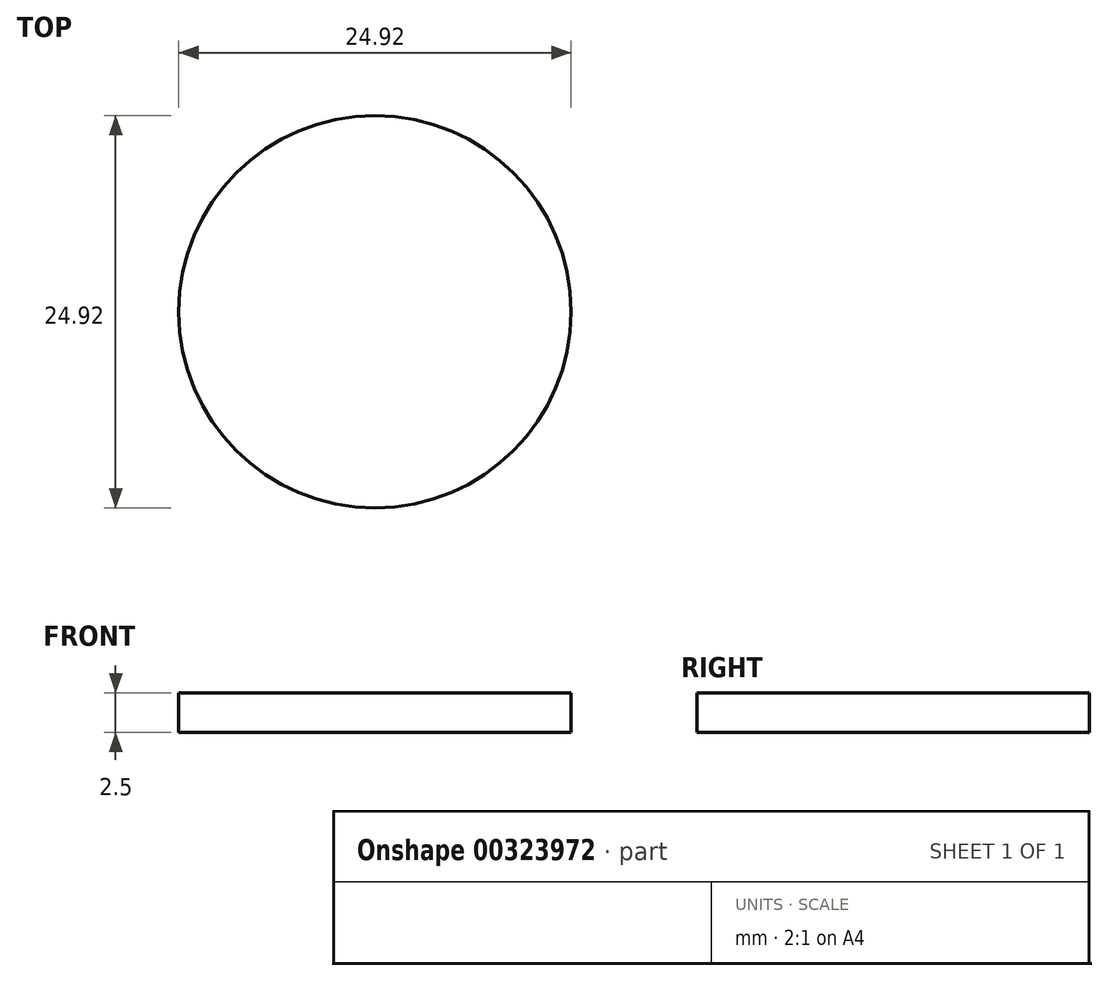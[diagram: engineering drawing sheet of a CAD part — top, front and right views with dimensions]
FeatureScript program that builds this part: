
annotation { "Feature Type Name" : "Feature", "Feature Type Description" : "" }
export const myFeature = defineFeature(function(context is Context, id is Id, definition is map)
    precondition{}
    {
        {
            var Q0;
            Q0=qCreatedBy(makeId("Top.planeOp"),FACE);
            var sketch = newSketch(context, id + "F0", { "sketchPlane" : qUnion([Q0])});
            skCircle(sketch, "E0", {"center": v(0, 0) * mm, "radius": 12.46 * mm});
            skPoint(sketch, "E1", {"position": v(-3.5, -4.1) * mm});
            skPoint(sketch, "E2", {"position": v(0.65, -7.87) * mm});
            skPoint(sketch, "E3", {"position": v(1.56, -1.75) * mm});
            skPoint(sketch, "E4", {"position": v(-1.48, -2.07) * mm});
            skPoint(sketch, "E5", {"position": v(3.08, 4) * mm});
            skPoint(sketch, "E6", {"position": v(-0.43, 3.54) * mm});
            skPoint(sketch, "E7", {"position": v(3.12, 10.12) * mm});
            skPoint(sketch, "E8", {"position": v(-6.33, 0.93) * mm});
            skPoint(sketch, "E9", {"position": v(-1.88, 1.74) * mm});
            skPoint(sketch, "E10", {"position": v(-7.66, -5.23) * mm});
            skPoint(sketch, "E11", {"position": v(-7.66, -9.83) * mm});
            skPoint(sketch, "E12", {"position": v(-1.56, -12.36) * mm});
            skPoint(sketch, "E13", {"position": v(-2.95, -8.3) * mm});
            skLineSegment(sketch, "E14", {"start": v(-1.56, -12.36) * mm, "end": v(0.65, -7.87) * mm});
            skLineSegment(sketch, "E15", {"start": v(-2.95, -8.3) * mm, "end": v(0.65, -7.87) * mm});
            skLineSegment(sketch, "E16", {"start": v(-2.95, -8.3) * mm, "end": v(1.56, -1.75) * mm});
            skLineSegment(sketch, "E17", {"start": v(1.56, -1.75) * mm, "end": v(-1.48, -2.07) * mm});
            skLineSegment(sketch, "E18", {"start": v(-1.48, -2.07) * mm, "end": v(3.08, 4) * mm});
            skLineSegment(sketch, "E19", {"start": v(3.08, 4) * mm, "end": v(-0.43, 3.54) * mm});
            skLineSegment(sketch, "E20", {"start": v(-0.43, 3.54) * mm, "end": v(3.12, 10.12) * mm});
            skLineSegment(sketch, "E21", {"start": v(3.12, 10.12) * mm, "end": v(-6.33, 0.93) * mm});
            skLineSegment(sketch, "E22", {"start": v(-6.33, 0.93) * mm, "end": v(-1.88, 1.74) * mm});
            skLineSegment(sketch, "E23", {"start": v(-1.88, 1.74) * mm, "end": v(-7.66, -5.23) * mm});
            skLineSegment(sketch, "E24", {"start": v(-7.66, -5.23) * mm, "end": v(-3.5, -4.1) * mm});
            skLineSegment(sketch, "E25", {"start": v(-3.5, -4.1) * mm, "end": v(-7.66, -9.83) * mm});
            skCircle(sketch, "E26", {"center": v(0, 0) * mm, "radius": 16.23 * mm});
            skSolve(sketch);
        }
        {
            var Q0;
            {var subQ0=sQuery(id+"F0.wireOp",EDGE,"E14");Q0=makeQuery(id+"F0.imprint","IMPRINT",FACE,{"disambiguationData":[TD([[makeQuery(id+"F0.imprint","IMPRINT",EDGE,{"derivedFrom":subQ0}),-1.0]])]});}
            var Q1;
            {var subQ0=sQuery(id+"F0.wireOp",EDGE,"E14");Q1=makeQuery(id+"F0.imprint","IMPRINT",FACE,{"disambiguationData":[TD([[makeQuery(id+"F0.imprint","IMPRINT",EDGE,{"derivedFrom":subQ0}),1.0]])]});}
            extrude(context, id + "F1", {"entities" : qUnion([Q0, Q1]), "depth" : 2.5 * mm});
        }
    });
